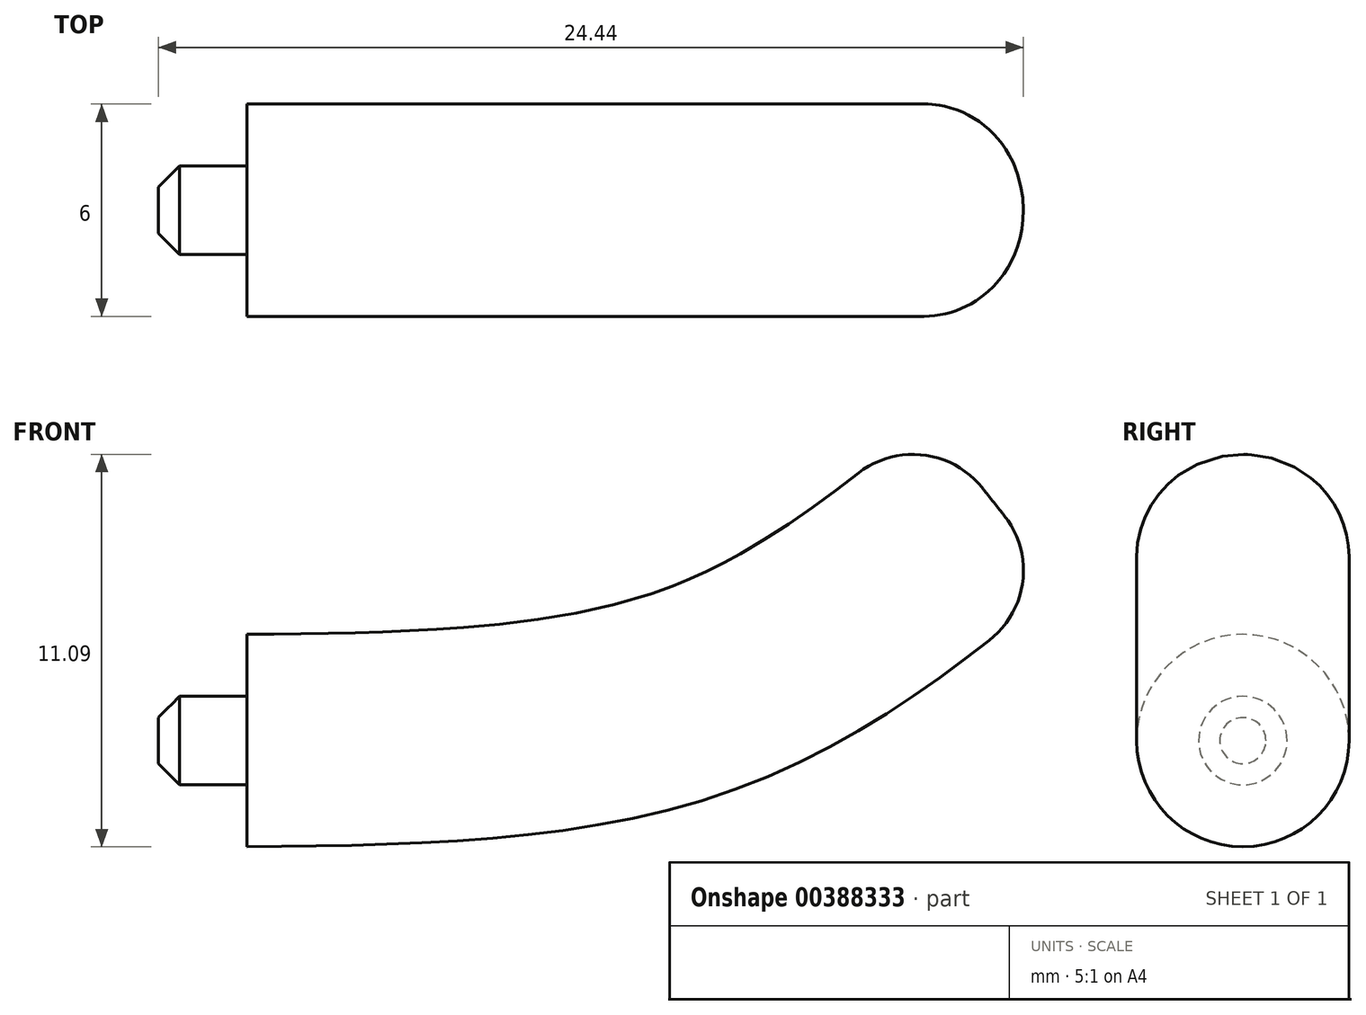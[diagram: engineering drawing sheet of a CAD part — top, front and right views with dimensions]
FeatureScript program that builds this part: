
annotation { "Feature Type Name" : "Feature", "Feature Type Description" : "" }
export const myFeature = defineFeature(function(context is Context, id is Id, definition is map)
    precondition{}
    {
        {
            var Q0;
            Q0=qCreatedBy(makeId("Right.planeOp"),FACE);
            var sketch = newSketch(context, id + "F0", { "sketchPlane" : qUnion([Q0])});
            skCircle(sketch, "E0", {"center": v(0, 0) * mm, "radius": 3 * mm});
            skSolve(sketch);
        }
        {
            var Q0;
            Q0=qCreatedBy(makeId("Front.planeOp"),FACE);
            var sketch = newSketch(context, id + "F1", { "sketchPlane" : qUnion([Q0])});
            skFitSpline(sketch, "E1", {"points": [v(0, 0) * mm, v(12.6, 1.38) * mm, v(21.08, 6.76) * mm], "startDerivative": vector(25.35, 0.27) * mm, "endDerivative": vector(16.64, 13.5) * mm});
            skSolve(sketch);
        }
        {
            var Q0;
            Q0 = qSketchRegion(id + "F0", true);
            var Q1;
            Q1 = qConstructionFilter(qBodyType(qCreatedBy(id + "F1" ,EDGE), BodyType.WIRE), ConstructionObject.NO);
            sweep(context, id + "F2", {"profiles" : qUnion([Q0]), "path" : qUnion([Q1])});
        }
        {
            var Q0;
            Q0=makeQuery(id+"F2.opSweep","CAP_EDGE",EDGE,{"disambiguationData":[OSD([sQuery(id+"F0.wireOp",EDGE,"E0"),sQuery(id+"F1.wireOp",VERTEX,"E1.end")])],"isStart":false});
            fillet(context, id + "F3", {"entities" : qUnion([Q0]), "radius" : 2.5 * mm, "tangentPropagation" : true, "allowEdgeOverflow" : false});
        }
        {
            var Q0;
            Q0=makeQuery(id+"F2.opSweep","CAP_FACE",FACE,{"disambiguationData":[OSD([sQuery(id+"F0.wireOp",EDGE,"E0"),sQuery(id+"F1.wireOp",VERTEX,"E1.start")])],"isStart":true});
            var sketch = newSketch(context, id + "F4", { "sketchPlane" : qUnion([Q0])});
            skCircle(sketch, "E2", {"center": v(0, 0) * mm, "radius": 1.25 * mm});
            skSolve(sketch);
        }
        {
            var Q0;
            Q0 = qSketchRegion(id + "F4", true);
            extrude(context, id + "F5", {"entities" : qUnion([Q0]), "operationType" : NewBodyOperationType.ADD, "depth" : 2.5 * mm});
        }
        {
            var Q0;
            Q0=makeQuery(id+"F5.opExtrude","CAP_EDGE",EDGE,{"disambiguationData":[OSD([sQuery(id+"F4.wireOp",EDGE,"E2")])],"isStart":false});
            chamfer(context, id + "F6", {"entities" : qUnion([Q0]), "width" : 0.6 * mm, "tangentPropagation" : true});
        }
    });
